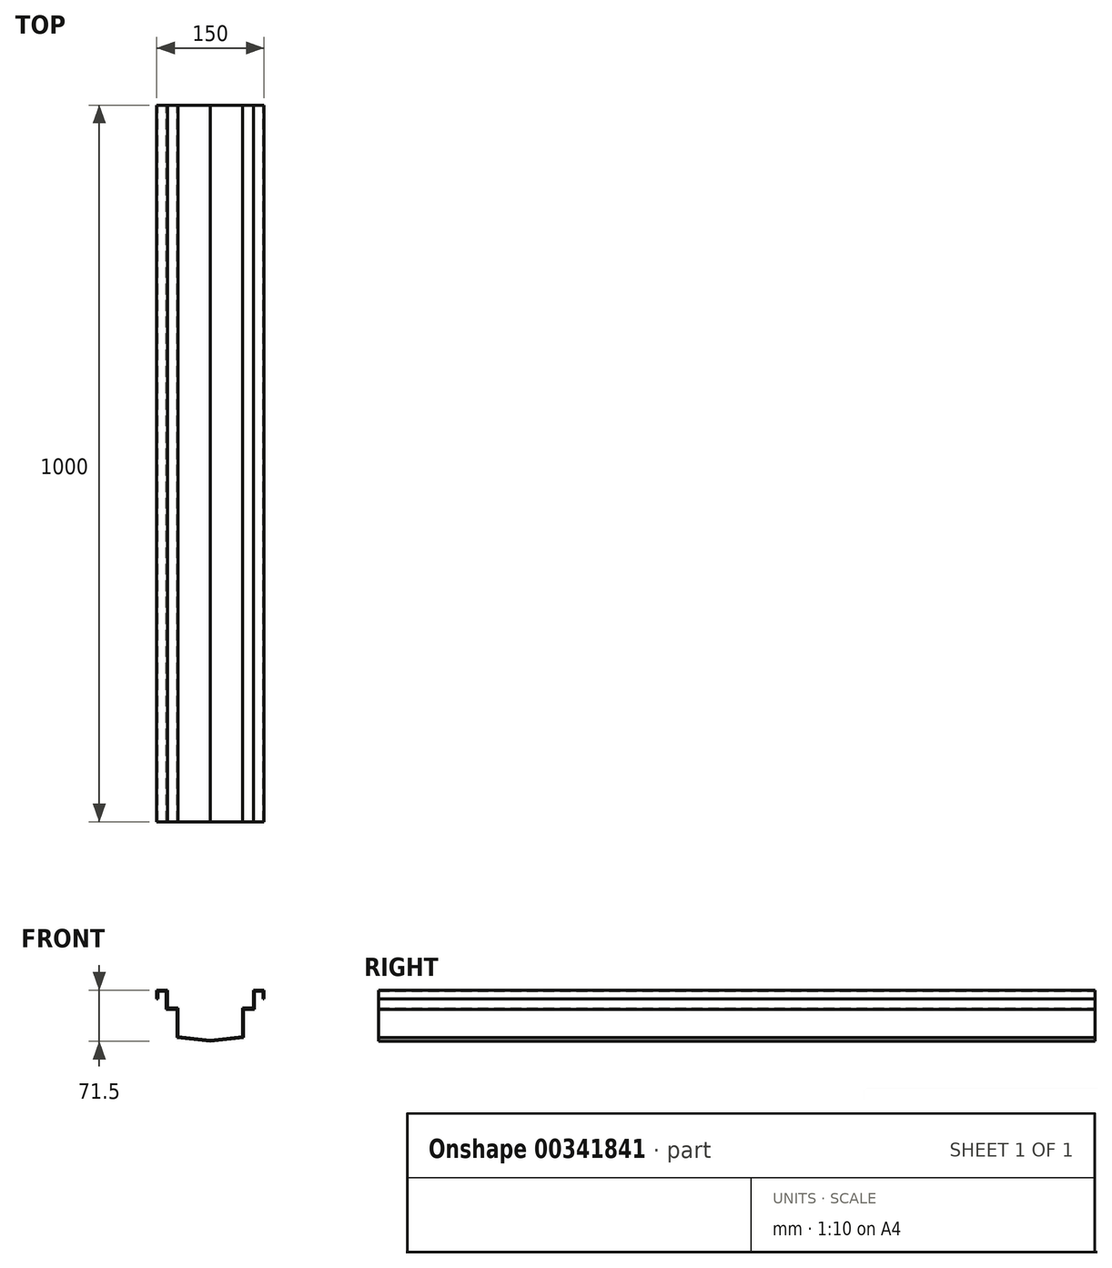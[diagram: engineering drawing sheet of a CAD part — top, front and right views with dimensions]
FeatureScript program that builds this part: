
annotation { "Feature Type Name" : "Feature", "Feature Type Description" : "" }
export const myFeature = defineFeature(function(context is Context, id is Id, definition is map)
    precondition{}
    {
        {
            var Q0;
            Q0=qCreatedBy(makeId("Front.planeOp"),FACE);
            var sketch = newSketch(context, id + "F0", { "sketchPlane" : qUnion([Q0])});
            skLineSegment(sketch, "E0", {"start": v(0, 0) * mm, "end": v(0, 12) * mm});
            skLineSegment(sketch, "E1", {"start": v(0, 12) * mm, "end": v(15, 12) * mm});
            skLineSegment(sketch, "E2", {"start": v(15, 12) * mm, "end": v(15, -13) * mm});
            skLineSegment(sketch, "E3", {"start": v(15, -13) * mm, "end": v(30, -13) * mm});
            skLineSegment(sketch, "E4", {"start": v(30, -13) * mm, "end": v(30, -53) * mm});
            skLineSegment(sketch, "E5", {"start": v(30, -53) * mm, "end": v(75, -58) * mm});
            skLineSegment(sketch, "E6", {"start": v(120, -53) * mm, "end": v(75, -58) * mm});
            skLineSegment(sketch, "E7", {"start": v(120, -53) * mm, "end": v(120, -13) * mm});
            skLineSegment(sketch, "E8", {"start": v(120, -13) * mm, "end": v(135, -13) * mm});
            skLineSegment(sketch, "E9", {"start": v(135, -13) * mm, "end": v(135, 12) * mm});
            skLineSegment(sketch, "E10", {"start": v(135, 12) * mm, "end": v(150, 12) * mm});
            skLineSegment(sketch, "E11", {"start": v(150, 12) * mm, "end": v(150, 0) * mm});
            skLineSegment(sketch, "E12", {"start": v(0, 0) * mm, "end": v(1.5, 0) * mm});
            skLineSegment(sketch, "E13", {"start": v(1.5, 0) * mm, "end": v(1.5, 10.5) * mm});
            skLineSegment(sketch, "E14", {"start": v(1.5, 10.5) * mm, "end": v(13.5, 10.5) * mm});
            skLineSegment(sketch, "E15", {"start": v(13.5, 10.5) * mm, "end": v(13.5, -14.5) * mm});
            skLineSegment(sketch, "E16", {"start": v(13.5, -14.5) * mm, "end": v(28.5, -14.5) * mm});
            skLineSegment(sketch, "E17", {"start": v(28.5, -14.5) * mm, "end": v(28.5, -54.5) * mm});
            skLineSegment(sketch, "E18", {"start": v(150, 0) * mm, "end": v(148.5, 0) * mm});
            skLineSegment(sketch, "E19", {"start": v(148.5, 0) * mm, "end": v(148.5, 10.5) * mm});
            skLineSegment(sketch, "E20", {"start": v(148.5, 10.5) * mm, "end": v(136.5, 10.5) * mm});
            skLineSegment(sketch, "E21", {"start": v(136.5, 10.5) * mm, "end": v(136.5, -14.5) * mm});
            skLineSegment(sketch, "E22", {"start": v(136.5, -14.5) * mm, "end": v(121.5, -14.5) * mm});
            skLineSegment(sketch, "E23", {"start": v(121.5, -14.5) * mm, "end": v(121.5, -54.5) * mm});
            skLineSegment(sketch, "E24", {"start": v(75, -59.5) * mm, "end": v(121.5, -54.5) * mm});
            skLineSegment(sketch, "E25", {"start": v(28.5, -54.5) * mm, "end": v(75, -59.5) * mm});
            skSolve(sketch);
        }
        {
            var Q0;
            Q0 = qSketchRegion(id + "F0", true);
            extrude(context, id + "F1", {"entities" : qUnion([Q0]), "depth" : 1000 * mm});
        }
    });
